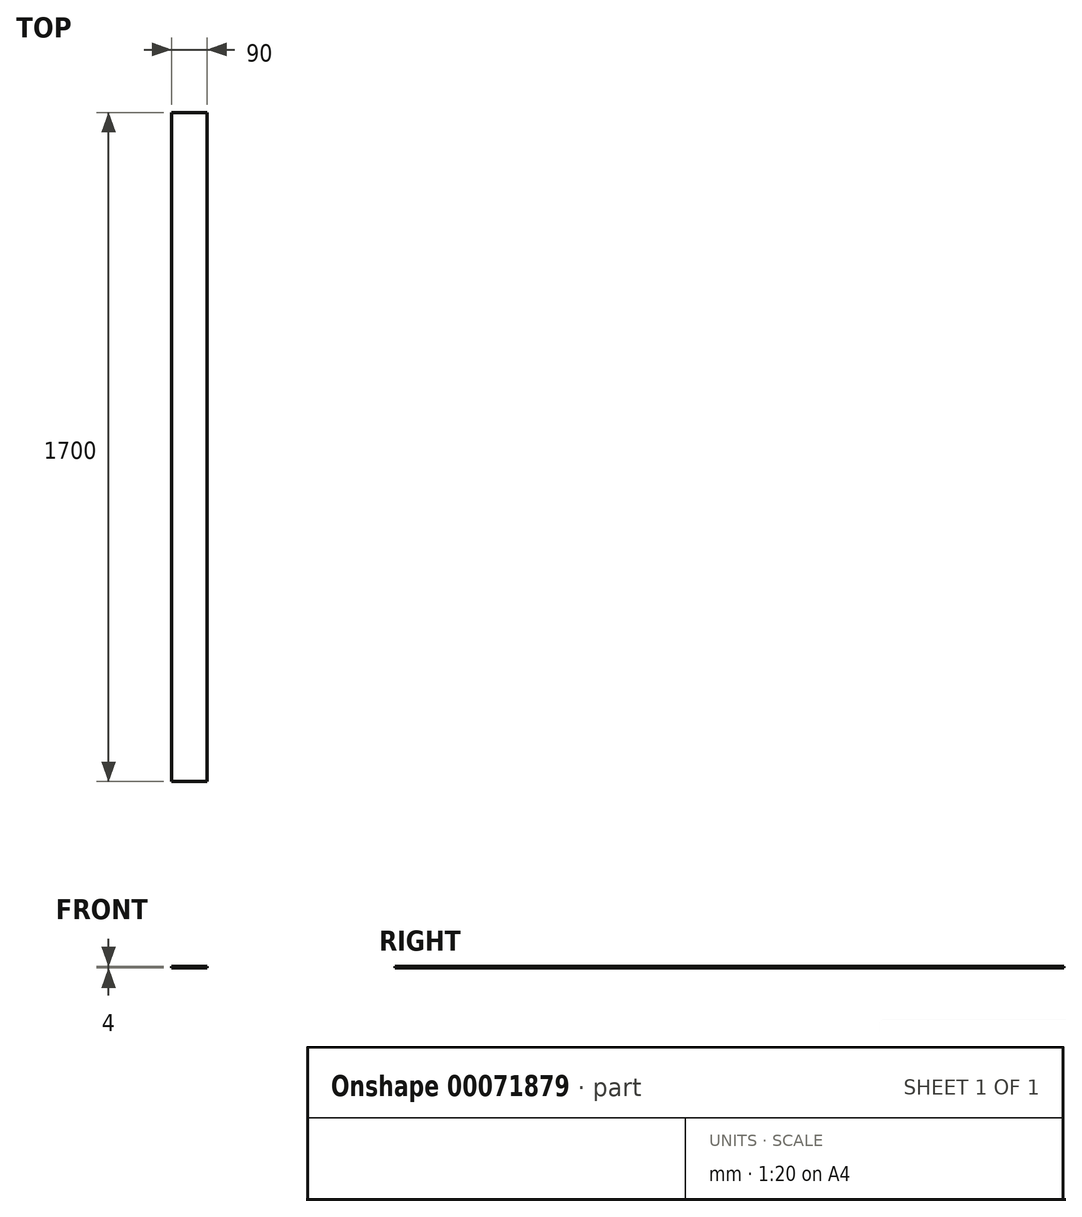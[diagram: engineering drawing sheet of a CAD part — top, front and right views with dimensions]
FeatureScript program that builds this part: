
annotation { "Feature Type Name" : "Feature", "Feature Type Description" : "" }
export const myFeature = defineFeature(function(context is Context, id is Id, definition is map)
    precondition{}
    {
        {
            var Q0;
            Q0=qCreatedBy(makeId("Top.planeOp"),FACE);
            var sketch = newSketch(context, id + "F0", { "sketchPlane" : qUnion([Q0])});
            skLineSegment(sketch, "E0.bottom", {"start": v(-45, -850) * mm, "end": v(45, -850) * mm});
            skLineSegment(sketch, "E0.top", {"start": v(-45, 850) * mm, "end": v(45, 850) * mm});
            skLineSegment(sketch, "E0.left", {"start": v(-45, -850) * mm, "end": v(-45, 850) * mm});
            skLineSegment(sketch, "E0.right", {"start": v(45, -850) * mm, "end": v(45, 850) * mm});
            skPoint(sketch, "E0.middle", {"position": v(0, 0) * mm});
            skSolve(sketch);
        }
        {
            var Q0;
            Q0=qSketchRegion(id+"F0",true);
            extrude(context, id + "F1", {"entities" : qUnion([Q0]), "depth" : 4 * mm});
        }
    });
